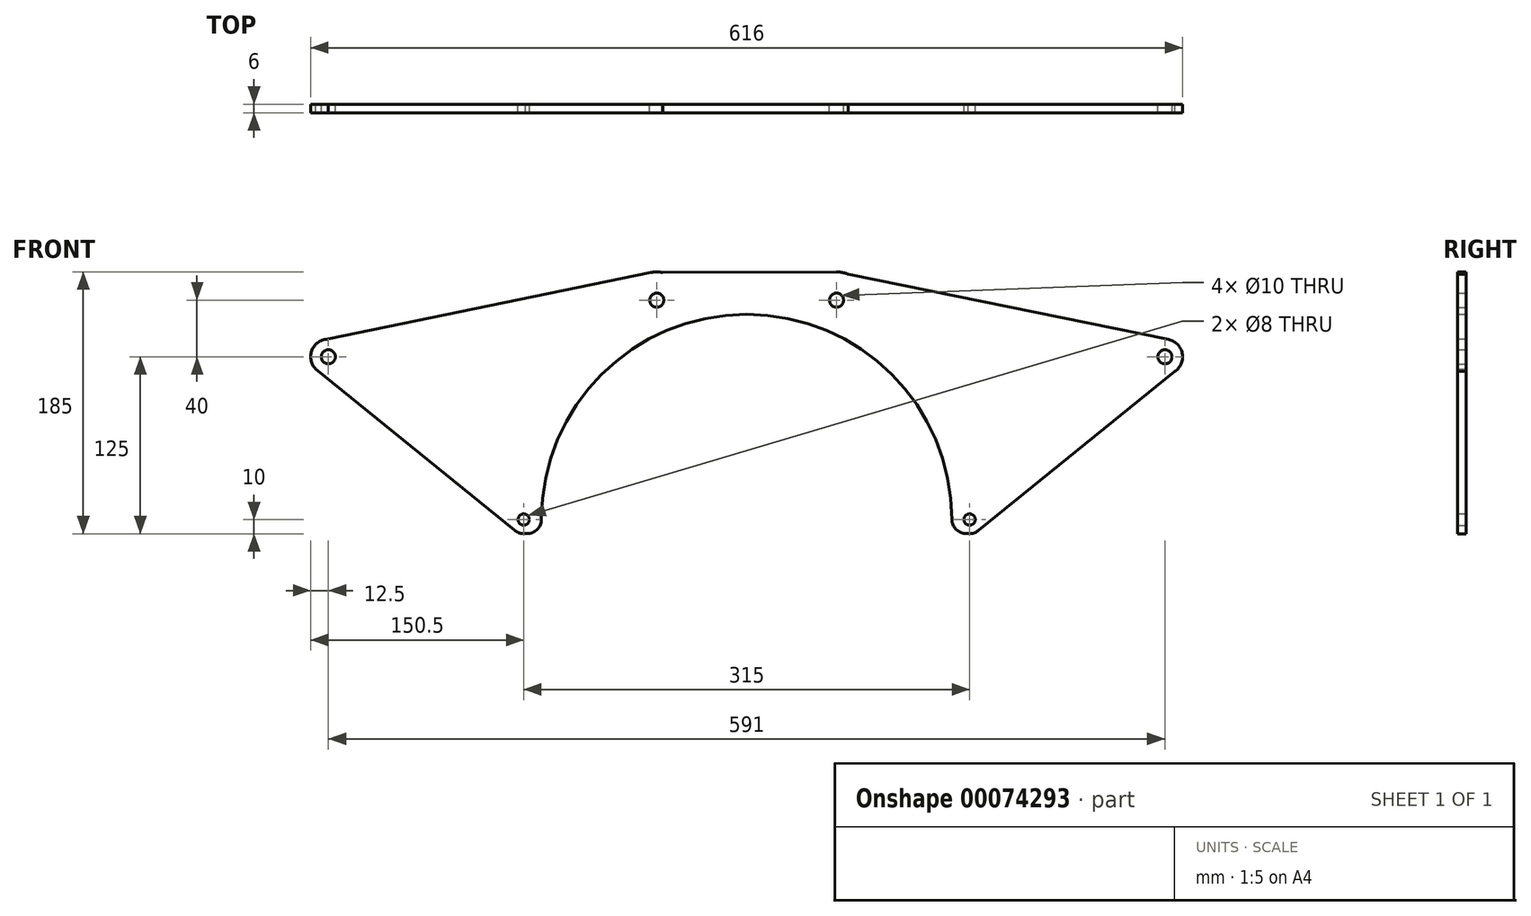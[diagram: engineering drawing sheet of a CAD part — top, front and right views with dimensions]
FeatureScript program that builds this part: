
annotation { "Feature Type Name" : "Feature", "Feature Type Description" : "" }
export const myFeature = defineFeature(function(context is Context, id is Id, definition is map)
    precondition{}
    {
        {
            var Q0;
            Q0=qCreatedBy(makeId("Front.planeOp"),FACE);
            var sketch = newSketch(context, id + "F0", { "sketchPlane" : qUnion([Q0])});
            skArc(sketch, "E0", {"start": v(144.7, -9.2) * mm, "mid": v(-0.36, 145) * mm, "end": v(-144.66, -9.91) * mm});
            skArc(sketch, "E1", {"start": v(156.52, -9.95) * mm, "mid": v(160.37, -9.58) * mm, "end": v(163.8, -7.77) * mm});
            skArc(sketch, "E2", {"start": v(-163.8, -7.77) * mm, "mid": v(-160.2, -9.63) * mm, "end": v(-156.16, -9.91) * mm});
            skArc(sketch, "E3", {"start": v(302.56, 104.68) * mm, "mid": v(307.75, 117.48) * mm, "end": v(297.99, 127.25) * mm});
            skArc(sketch, "E4", {"start": v(-295.5, 127.5) * mm, "mid": v(-306.96, 119.98) * mm, "end": v(-304.64, 106.48) * mm});
            skArc(sketch, "E5", {"start": v(71.73, 173.23) * mm, "mid": v(67.68, 174.56) * mm, "end": v(63.43, 175) * mm});
            skArc(sketch, "E6", {"start": v(-59.52, 174.6) * mm, "mid": v(-63.53, 175) * mm, "end": v(-67.55, 174.59) * mm});
            skLineSegment(sketch, "E7", {"start": v(-295.5, 127.5) * mm, "end": v(-67.55, 174.59) * mm});
            skLineSegment(sketch, "E8", {"start": v(-63.5, 174.59) * mm, "end": v(63.5, 175) * mm});
            skLineSegment(sketch, "E9", {"start": v(71.73, 173.23) * mm, "end": v(297.99, 127.25) * mm});
            skLineSegment(sketch, "E10", {"start": v(304.13, 105.96) * mm, "end": v(163.8, -7.77) * mm});
            skLineSegment(sketch, "E11", {"start": v(-304.64, 106.48) * mm, "end": v(-163.8, -7.77) * mm});
            skLineSegment(sketch, "E12", {"start": v(-158.84, -9.9) * mm, "end": v(-144.66, -9.91) * mm});
            skLineSegment(sketch, "E13", {"start": v(157.2, -10) * mm, "end": v(144.7, -9.2) * mm});
            skCircle(sketch, "E14", {"center": v(-295.5, 115) * mm, "radius": 5 * mm});
            skCircle(sketch, "E15", {"center": v(-63.5, 155) * mm, "radius": 5 * mm});
            skCircle(sketch, "E16", {"center": v(63.5, 155) * mm, "radius": 5 * mm});
            skCircle(sketch, "E17", {"center": v(295.5, 115) * mm, "radius": 5 * mm});
            skCircle(sketch, "E18", {"center": v(157.5, 0) * mm, "radius": 4 * mm});
            skCircle(sketch, "E19", {"center": v(-157.5, 0) * mm, "radius": 4 * mm});
            skSolve(sketch);
        }
        {
            var Q0;
            Q0 = qSketchRegion(id + "F0", true);
            extrude(context, id + "F1", {"entities" : qUnion([Q0]), "depth" : 6 * mm});
        }
        {
            var Q0;
            Q0=makeQuery(id+"F1.opExtrude","SWEPT_EDGE",EDGE,{"disambiguationData":[OSD([sQuery(id+"F0.wireOp",EDGE,"E0"),sQuery(id+"F0.wireOp",EDGE,"E12")])]});
            var Q1;
            Q1=makeQuery(id+"F1.opExtrude","SWEPT_EDGE",EDGE,{"disambiguationData":[OSD([sQuery(id+"F0.wireOp",EDGE,"E0"),sQuery(id+"F0.wireOp",EDGE,"E13")])]});
            fillet(context, id + "F2", {"entities" : qUnion([Q0, Q1]), "radius" : 10 * mm, "tangentPropagation" : true, "allowEdgeOverflow" : false});
        }
    });
